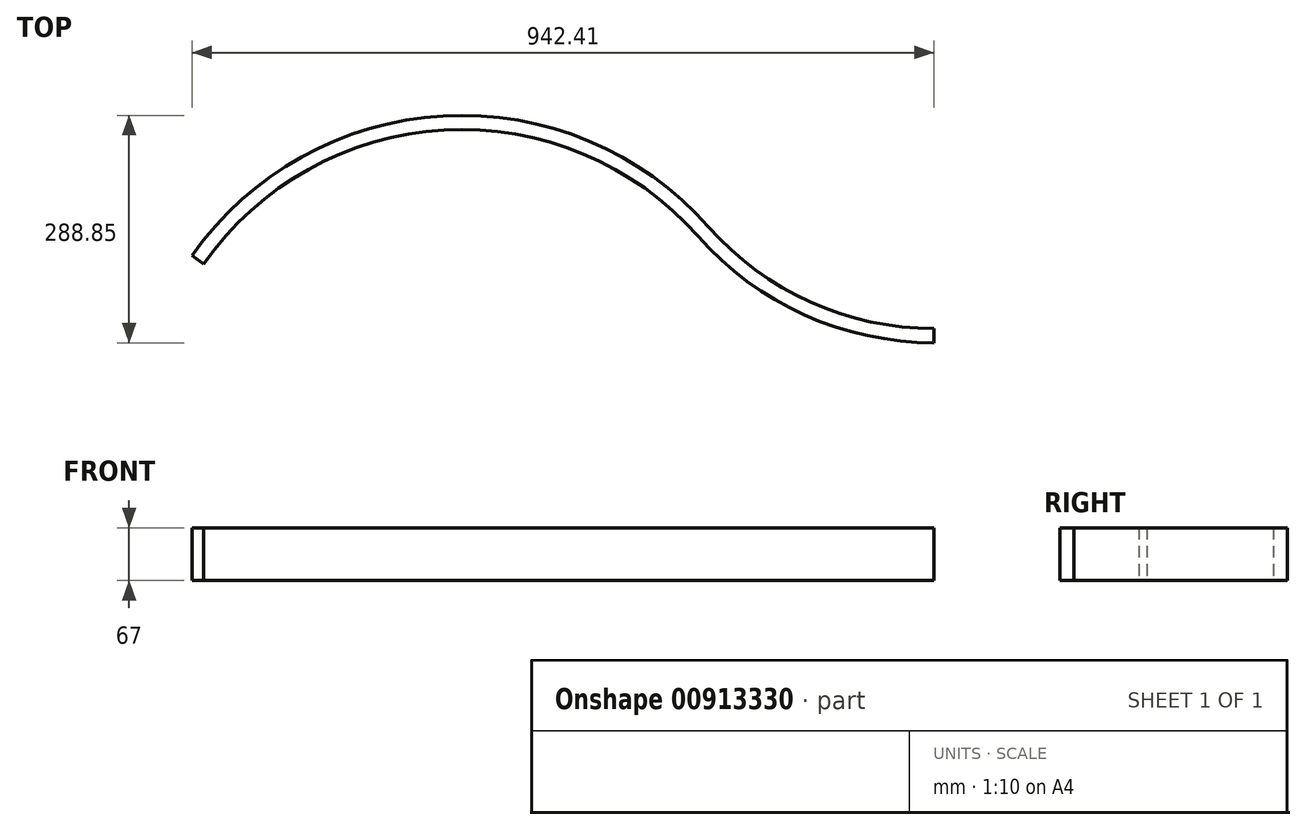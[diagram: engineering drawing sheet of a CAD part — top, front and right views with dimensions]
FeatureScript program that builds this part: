
annotation { "Feature Type Name" : "Feature", "Feature Type Description" : "" }
export const myFeature = defineFeature(function(context is Context, id is Id, definition is map)
    precondition{}
    {
        {
            var Q0;
            Q0=qCreatedBy(makeId("Top.planeOp"),FACE);
            var sketch = newSketch(context, id + "F0", { "sketchPlane" : qUnion([Q0])});
            skArc(sketch, "E0", {"start": v(300, 264.58) * mm, "mid": v(-22.36, 399.37) * mm, "end": v(-327.66, 229.43) * mm});
            skArc(sketch, "E1", {"start": v(300, 264.58) * mm, "mid": v(435.42, 164.58) * mm, "end": v(600, 129.15) * mm});
            skLineSegment(sketch, "E2", {"start": v(600, 529.15) * mm, "end": v(600, 129.15) * mm, "construction": true});
            skLineSegment(sketch, "E3", {"start": v(-1346.7, 0) * mm, "end": v(2582.15, 0) * mm, "construction": true});
            skArc(sketch, "E4", {"start": v(313.5, 276.48) * mm, "mid": v(-23.37, 417.35) * mm, "end": v(-342.4, 239.75) * mm});
            skArc(sketch, "E5", {"start": v(313.5, 276.48) * mm, "mid": v(442.83, 180.98) * mm, "end": v(600, 147.15) * mm});
            skLineSegment(sketch, "E6", {"start": v(-342.4, 239.75) * mm, "end": v(-327.66, 229.43) * mm});
            skLineSegment(sketch, "E7", {"start": v(600, 147.15) * mm, "end": v(600, 129.15) * mm});
            skLineSegment(sketch, "E8", {"start": v(-327.66, 229.43) * mm, "end": v(0, 0) * mm, "construction": true});
            skArc(sketch, "E9", {"start": v(-327.66, 229.43) * mm, "mid": v(-400, 0) * mm, "end": v(-327.66, -229.43) * mm});
            skArc(sketch, "E10", {"start": v(-342.4, 239.75) * mm, "mid": v(-418, 0) * mm, "end": v(-342.4, -239.75) * mm});
            skLineSegment(sketch, "E11", {"start": v(0, 0) * mm, "end": v(-327.66, -229.43) * mm, "construction": true});
            skLineSegment(sketch, "E12", {"start": v(-342.4, -239.75) * mm, "end": v(-327.66, -229.43) * mm});
            skArc(sketch, "E13", {"start": v(-327.66, -229.43) * mm, "mid": v(-22.36, -399.37) * mm, "end": v(300, -264.58) * mm});
            skArc(sketch, "E14", {"start": v(-342.4, -239.75) * mm, "mid": v(-23.37, -417.35) * mm, "end": v(313.5, -276.48) * mm});
            skArc(sketch, "E15", {"start": v(600, -147.15) * mm, "mid": v(442.83, -180.98) * mm, "end": v(313.5, -276.48) * mm});
            skLineSegment(sketch, "E16", {"start": v(600, -529.15) * mm, "end": v(600, -147.15) * mm, "construction": true});
            skArc(sketch, "E17", {"start": v(600, -129.15) * mm, "mid": v(435.42, -164.58) * mm, "end": v(300, -264.58) * mm});
            skLineSegment(sketch, "E18", {"start": v(600, -129.15) * mm, "end": v(600, -147.15) * mm});
            skSolve(sketch);
        }
        {
            var Q0;
            Q0=makeQuery(id+"F0.imprint","IMPRINT",FACE,{"disambiguationData":[TD([[makeQuery(id+"F0.imprint","IMPRINT",EDGE,{"derivedFrom":sQuery(id+"F0.wireOp",EDGE,"E0")}),-1.0]])]});
            extrude(context, id + "F1", {"entities" : qUnion([Q0]), "depth" : 67 * mm, "offsetDistance" : 25 * mm});
        }
    });
